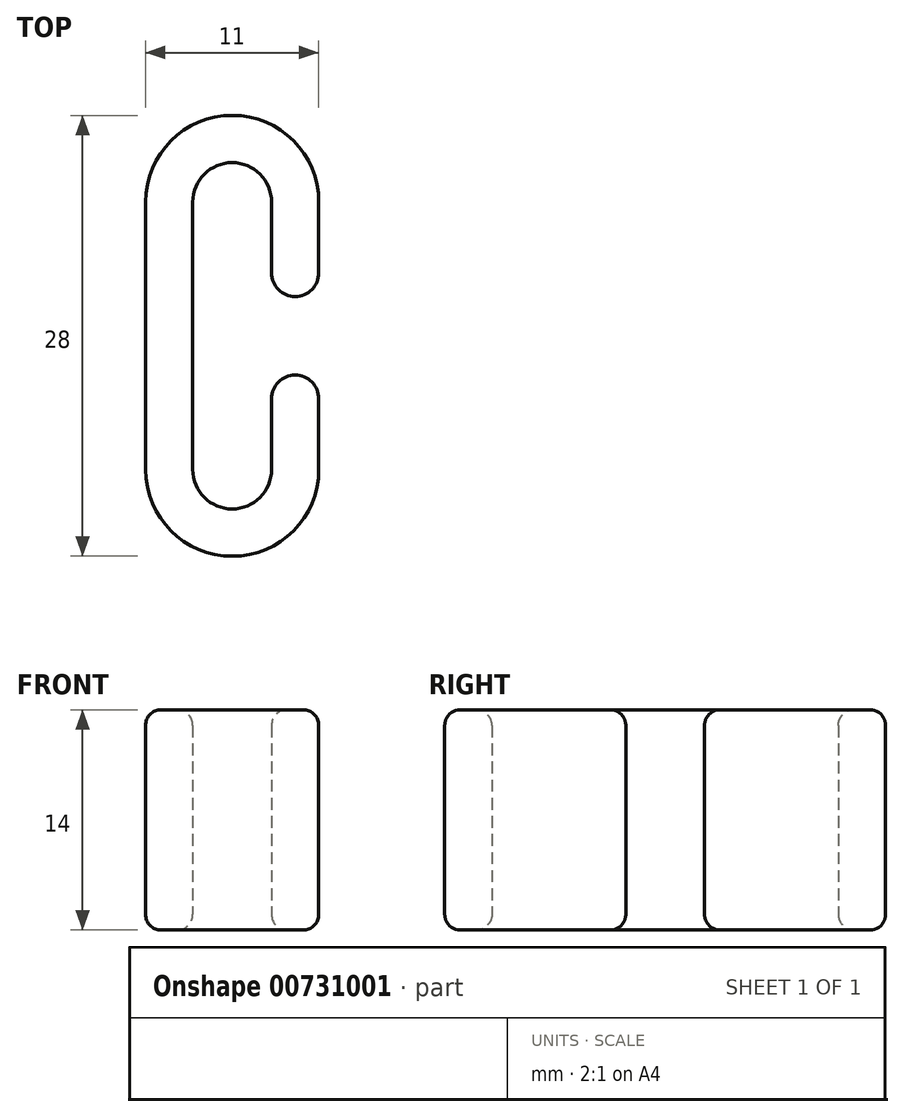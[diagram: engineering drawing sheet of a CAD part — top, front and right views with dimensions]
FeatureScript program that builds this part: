
annotation { "Feature Type Name" : "Feature", "Feature Type Description" : "" }
export const myFeature = defineFeature(function(context is Context, id is Id, definition is map)
    precondition{}
    {
        {
            var Q0;
            Q0=qCreatedBy(makeId("Top.planeOp"),FACE);
            var sketch = newSketch(context, id + "F0", { "sketchPlane" : qUnion([Q0])});
            skLineSegment(sketch, "E0", {"start": v(0, 0) * mm, "end": v(0, 8.5) * mm});
            skLineSegment(sketch, "E1", {"start": v(24.07, 0) * mm, "end": v(-34.6, 0) * mm, "construction": true});
            skArc(sketch, "E2", {"start": v(5, 8.5) * mm, "mid": v(2.5, 11) * mm, "end": v(0, 8.5) * mm});
            skLineSegment(sketch, "E3", {"start": v(5, 8.5) * mm, "end": v(5, 4) * mm});
            skLineSegment(sketch, "E4.0", {"start": v(8, 8.5) * mm, "end": v(8, 4) * mm});
            skArc(sketch, "E4.1", {"start": v(8, 8.5) * mm, "mid": v(2.5, 14) * mm, "end": v(-3, 8.5) * mm});
            skLineSegment(sketch, "E4.2", {"start": v(-3, 0) * mm, "end": v(-3, 8.5) * mm});
            skArc(sketch, "E5", {"start": v(5, 4) * mm, "mid": v(6.5, 2.5) * mm, "end": v(8, 4) * mm});
            skLineSegment(sketch, "E6.MirrorCS", {"start": v(0, 0) * mm, "end": v(0, -8.5) * mm});
            skArc(sketch, "E7.MirrorCS", {"start": v(5, -8.5) * mm, "mid": v(2.5, -11) * mm, "end": v(0, -8.5) * mm});
            skLineSegment(sketch, "E8.MirrorCS", {"start": v(5, -8.5) * mm, "end": v(5, -4) * mm});
            skLineSegment(sketch, "E9.MirrorCS", {"start": v(8, -8.5) * mm, "end": v(8, -4) * mm});
            skArc(sketch, "E10.MirrorCS", {"start": v(8, -8.5) * mm, "mid": v(2.5, -14) * mm, "end": v(-3, -8.5) * mm});
            skLineSegment(sketch, "E11.MirrorCS", {"start": v(-3, 0) * mm, "end": v(-3, -8.5) * mm});
            skArc(sketch, "E12.MirrorCS", {"start": v(5, -4) * mm, "mid": v(6.5, -2.5) * mm, "end": v(8, -4) * mm});
            skSolve(sketch);
        }
        {
            var Q0;
            Q0 = qSketchRegion(id + "F0", true);
            extrude(context, id + "F1", {"entities" : qUnion([Q0]), "depth" : 14 * mm, "offsetDistance" : 25 * mm});
        }
        {
            var Q0;
            Q0=makeQuery(id+"F1.opExtrude","CAP_FACE",FACE,{"disambiguationData":[OSD([sQuery(id+"F0.wireOp",EDGE,"E0"),sQuery(id+"F0.wireOp",EDGE,"E2"),sQuery(id+"F0.wireOp",EDGE,"E3"),sQuery(id+"F0.wireOp",EDGE,"E4.0"),sQuery(id+"F0.wireOp",EDGE,"E4.1"),sQuery(id+"F0.wireOp",EDGE,"E4.2"),sQuery(id+"F0.wireOp",EDGE,"E5"),sQuery(id+"F0.wireOp",EDGE,"E6.MirrorCS"),sQuery(id+"F0.wireOp",EDGE,"E7.MirrorCS"),sQuery(id+"F0.wireOp",EDGE,"E8.MirrorCS"),sQuery(id+"F0.wireOp",EDGE,"E9.MirrorCS"),sQuery(id+"F0.wireOp",EDGE,"E10.MirrorCS"),sQuery(id+"F0.wireOp",EDGE,"E11.MirrorCS"),sQuery(id+"F0.wireOp",EDGE,"E12.MirrorCS")])],"isStart":false});
            var Q1;
            Q1=makeQuery(id+"F1.opExtrude","CAP_FACE",FACE,{"disambiguationData":[OSD([sQuery(id+"F0.wireOp",EDGE,"E0"),sQuery(id+"F0.wireOp",EDGE,"E2"),sQuery(id+"F0.wireOp",EDGE,"E3"),sQuery(id+"F0.wireOp",EDGE,"E4.0"),sQuery(id+"F0.wireOp",EDGE,"E4.1"),sQuery(id+"F0.wireOp",EDGE,"E4.2"),sQuery(id+"F0.wireOp",EDGE,"E5"),sQuery(id+"F0.wireOp",EDGE,"E6.MirrorCS"),sQuery(id+"F0.wireOp",EDGE,"E7.MirrorCS"),sQuery(id+"F0.wireOp",EDGE,"E8.MirrorCS"),sQuery(id+"F0.wireOp",EDGE,"E9.MirrorCS"),sQuery(id+"F0.wireOp",EDGE,"E10.MirrorCS"),sQuery(id+"F0.wireOp",EDGE,"E11.MirrorCS"),sQuery(id+"F0.wireOp",EDGE,"E12.MirrorCS")])],"isStart":true});
            fillet(context, id + "F2", {"entities" : qUnion([Q0, Q1]), "radius" : 1 * mm, "tangentPropagation" : true, "allowEdgeOverflow" : false});
        }
    });
